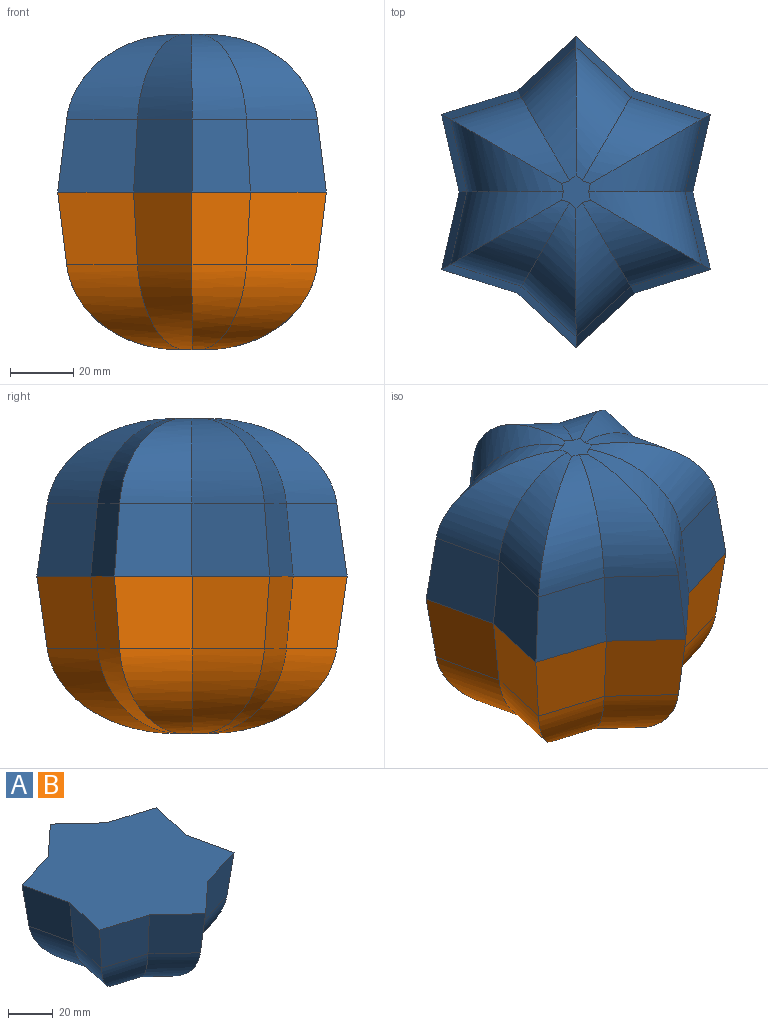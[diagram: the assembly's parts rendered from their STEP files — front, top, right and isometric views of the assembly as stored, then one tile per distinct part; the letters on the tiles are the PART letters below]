
ASSEMBLY  parts=2 mates=1
PART A: 26 faces, bbox 85.3x98.5x50 mm
  f0: plane 98.49x85.29mm, normal (0,0,1), area 5475.5mm2, adj f1,f2,f3,f4,f5,f6,f7,f8
  f1: plane 25.36x23.14mm, normal (-0.29,-0.95,-0.1), area 567.6mm2, adj f0,f2,f12,f22
  f2: plane 23.14x19.3mm, normal (-0.68,-0.73,-0.1), area 567.5mm2, adj f0,f1,f3,f20
  f3: plane 23.14x19.31mm, normal (0.68,-0.73,-0.1), area 567.6mm2, adj f0,f2,f4,f18
  f4: plane 25.36x23.14mm, normal (0.29,-0.95,-0.1), area 567.5mm2, adj f0,f3,f5,f16
  f5: plane 24.62x23.14mm, normal (0.97,0.22,-0.1), area 567.6mm2, adj f0,f4,f6,f14
  f6: plane 24.62x23.14mm, normal (0.97,-0.22,-0.1), area 567.5mm2, adj f0,f5,f7,f15
  f7: plane 25.36x23.14mm, normal (0.29,0.95,-0.1), area 567.6mm2, adj f0,f6,f8,f17
  f8: plane 23.14x19.3mm, normal (0.68,0.73,-0.1), area 567.5mm2, adj f0,f7,f9,f19
  f9: plane 23.14x19.31mm, normal (-0.68,0.73,-0.1), area 567.6mm2, adj f0,f8,f10,f21
  f10: plane 25.36x23.14mm, normal (-0.29,0.95,-0.1), area 567.5mm2, adj f0,f9,f11,f23
  f11: plane 24.62x23.14mm, normal (-0.97,-0.22,-0.1), area 567.6mm2, adj f0,f10,f12,f25
  f12: plane 24.62x23.14mm, normal (-0.97,0.22,-0.1), area 567.5mm2, adj f0,f1,f11,f24
  f13: plane 10.57x9.15mm, normal (0,0,-1), area 63.1mm2, adj f14,f15,f16,f17,f18,f19,f20,f21
  f14: cylinder r=30mm len=36.16mm, axis (0.22,-0.98,0), area 682.1mm2, adj f5,f13,f15,f16
  f15: cylinder r=30mm len=36.16mm, axis (-0.22,-0.98,0), area 682mm2, adj f6,f13,f14,f17
  f16: cylinder r=30mm len=37.79mm, axis (-0.96,-0.3,0), area 682mm2, adj f4,f13,f14,f18
  f17: cylinder r=30mm len=37.79mm, axis (0.96,-0.3,0), area 682.1mm2, adj f7,f13,f15,f19
  f18: cylinder r=30mm len=42.51mm, axis (-0.73,-0.68,0), area 682.1mm2, adj f3,f13,f16,f20
  f19: cylinder r=30mm len=42.51mm, axis (0.73,-0.68,0), area 682mm2, adj f8,f13,f17,f21
  f20: cylinder r=30mm len=42.51mm, axis (-0.73,0.68,0), area 682mm2, adj f2,f13,f18,f22
  f21: cylinder r=30mm len=42.51mm, axis (0.73,0.68,0), area 682.1mm2, adj f9,f13,f19,f23
  f22: cylinder r=30mm len=37.79mm, axis (-0.96,0.3,0), area 682.1mm2, adj f1,f13,f20,f24
  f23: cylinder r=30mm len=37.79mm, axis (0.96,0.3,0), area 682mm2, adj f10,f13,f21,f25
  f24: cylinder r=30mm len=36.16mm, axis (0.22,0.98,0), area 682mm2, adj f12,f13,f22,f25
  f25: cylinder r=30mm len=36.16mm, axis (-0.22,0.98,0), area 682.1mm2, adj f11,f13,f23,f24
PART B: same geometry as A
PLACE A rot(axis=(1,0,0),180deg) t=(13.98,3.72,-11.53)mm
PLACE B t=(13.98,3.72,48.47)mm
MATE fastened A.f0 <-> B.f0  axis (0,0,-1) through (13.98,3.72,18.47)mm
